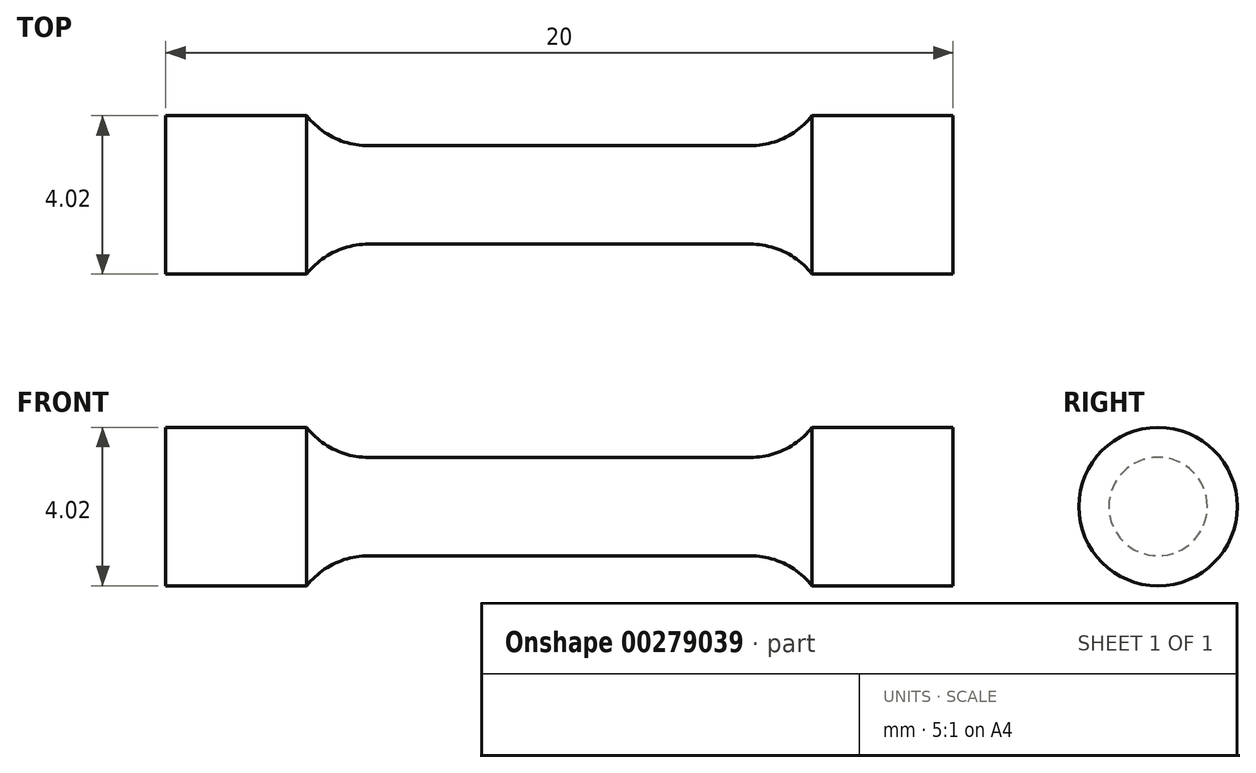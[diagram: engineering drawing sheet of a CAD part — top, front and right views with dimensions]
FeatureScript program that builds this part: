
annotation { "Feature Type Name" : "Feature", "Feature Type Description" : "" }
export const myFeature = defineFeature(function(context is Context, id is Id, definition is map)
    precondition{}
    {
        {
            var Q0;
            Q0=qCreatedBy(makeId("Front.planeOp"),FACE);
            var sketch = newSketch(context, id + "F0", { "sketchPlane" : qUnion([Q0])});
            skLineSegment(sketch, "E0", {"start": v(0, 1.25) * mm, "end": v(4.85, 1.25) * mm});
            skArc(sketch, "E1", {"start": v(4.85, 1.25) * mm, "mid": v(5.72, 1.45) * mm, "end": v(6.42, 2.01) * mm});
            skLineSegment(sketch, "E2", {"start": v(6.42, 2.01) * mm, "end": v(10, 2.01) * mm});
            skLineSegment(sketch, "E3", {"start": v(10, 2.01) * mm, "end": v(10, 0) * mm});
            skLineSegment(sketch, "E4.MirrorCS", {"start": v(0, 1.25) * mm, "end": v(-4.85, 1.25) * mm});
            skLineSegment(sketch, "E5.MirrorCS", {"start": v(-10, 2.01) * mm, "end": v(-10, 0) * mm});
            skLineSegment(sketch, "E6.MirrorCS", {"start": v(-6.42, 2.01) * mm, "end": v(-10, 2.01) * mm});
            skArc(sketch, "E7.MirrorCS", {"start": v(-4.85, 1.25) * mm, "mid": v(-5.72, 1.45) * mm, "end": v(-6.42, 2.01) * mm});
            skLineSegment(sketch, "E8", {"start": v(-10, 0) * mm, "end": v(10, 0) * mm});
            skSolve(sketch);
        }
        {
            var Q0;
            Q0=makeQuery(id+"F0.imprint","IMPRINT",FACE,{"disambiguationData":[TD([[makeQuery(id+"F0.imprint","IMPRINT",EDGE,{"derivedFrom":sQuery(id+"F0.wireOp",EDGE,"E0")}),-1.0]])]});
            var Q1;
            Q1=sQuery(id+"F0.wireOp",EDGE,"E8");
            revolve(context, id + "F1", {"entities" : qUnion([Q0]), "axis" : qUnion([Q1]), "revolveType" : RevolveType.FULL});
        }
    });
